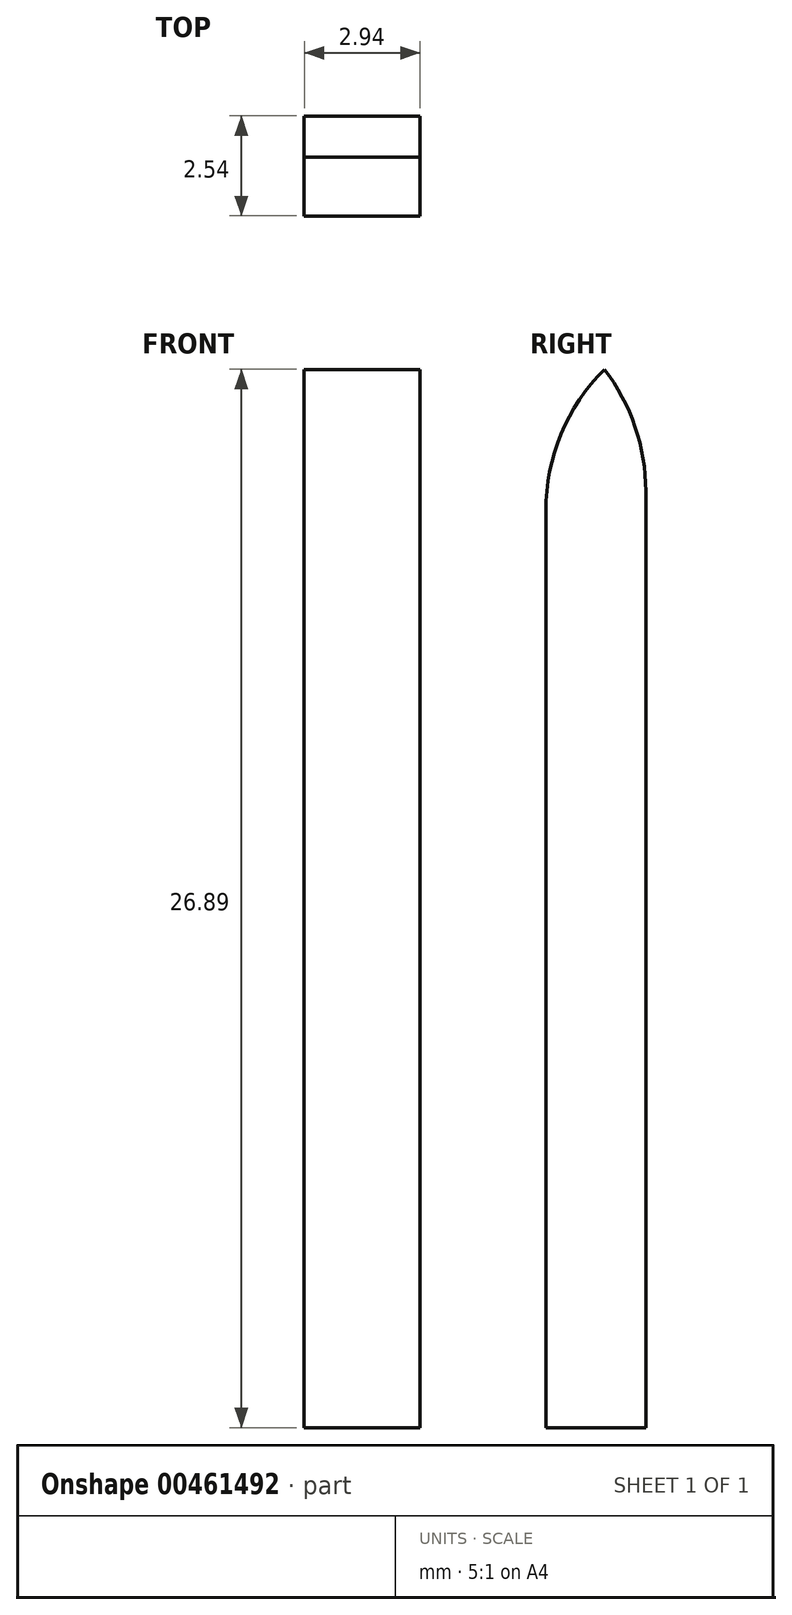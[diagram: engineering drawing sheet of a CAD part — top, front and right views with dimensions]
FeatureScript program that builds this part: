
annotation { "Feature Type Name" : "Feature", "Feature Type Description" : "" }
export const myFeature = defineFeature(function(context is Context, id is Id, definition is map)
    precondition{}
    {
        {
            var Q0;
            Q0=qCreatedBy(makeId("Top.planeOp"),FACE);
            var sketch = newSketch(context, id + "F0", { "sketchPlane" : qUnion([Q0])});
            skLineSegment(sketch, "E0.bottom", {"start": v(-38.1, 44.3) * mm, "end": v(-35.15, 44.3) * mm});
            skLineSegment(sketch, "E0.top", {"start": v(-38.1, 41.77) * mm, "end": v(-35.15, 41.77) * mm});
            skLineSegment(sketch, "E0.left", {"start": v(-38.1, 44.3) * mm, "end": v(-38.1, 41.77) * mm});
            skLineSegment(sketch, "E0.right", {"start": v(-35.15, 44.3) * mm, "end": v(-35.15, 41.77) * mm});
            skSolve(sketch);
        }
        {
            var Q0;
            Q0=makeQuery(id+"F0.imprint","IMPRINT",FACE,{"disambiguationData":[TD([[makeQuery(id+"F0.imprint","IMPRINT",EDGE,{"derivedFrom":sQuery(id+"F0.wireOp",EDGE,"E0.bottom")}),-1.0]])]});
            extrude(context, id + "F1", {"entities" : qUnion([Q0]), "depth" : 38.1 * mm});
        }
        {
            var Q0;
            Q0=makeQuery(id+"F1.opExtrude","CAP_EDGE",EDGE,{"disambiguationData":[OSD([sQuery(id+"F0.wireOp",EDGE,"E0.top")])],"isStart":false});
            chamfer(context, id + "F2", {"entities" : qUnion([Q0]), "width" : 12.7 * mm, "tangentPropagation" : true});
        }
        {
            var Q0;
            {var subQ0=sQuery(id+"F0.wireOp",EDGE,"E0.top");Q0=makeQuery(id+"F2.opChamfer","BLEND_EDGE",EDGE,{"blendedFrom":[makeQuery(id+"F1.opExtrude","CAP_EDGE",EDGE,{"disambiguationData":[OSD([subQ0])],"isStart":false}),makeQuery(id+"F1.opExtrude","SWEPT_FACE",FACE,{"disambiguationData":[OSD([subQ0])]})],"blendedInto":[makeQuery(id+"F1.opExtrude","SWEPT_FACE",FACE,{"disambiguationData":[OSD([subQ0])]})]});}
            fillet(context, id + "F3", {"entities" : qUnion([Q0]), "radius" : 5.08 * mm, "tangentPropagation" : true, "allowEdgeOverflow" : false});
        }
        {
            var Q0;
            Q0=makeQuery(id+"F2.opChamfer","BLEND_EDGE",EDGE,{"blendedFrom":[makeQuery(id+"F1.opExtrude","CAP_EDGE",EDGE,{"disambiguationData":[OSD([sQuery(id+"F0.wireOp",EDGE,"E0.top")])],"isStart":false}),makeQuery(id+"F1.opExtrude","SWEPT_FACE",FACE,{"disambiguationData":[OSD([sQuery(id+"F0.wireOp",EDGE,"E0.bottom")])]})],"blendedInto":[makeQuery(id+"F1.opExtrude","SWEPT_FACE",FACE,{"disambiguationData":[OSD([sQuery(id+"F0.wireOp",EDGE,"E0.bottom")])]})]});
            fillet(context, id + "F4", {"entities" : qUnion([Q0]), "radius" : 5.08 * mm, "tangentPropagation" : true, "allowEdgeOverflow" : false});
        }
    });
